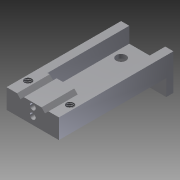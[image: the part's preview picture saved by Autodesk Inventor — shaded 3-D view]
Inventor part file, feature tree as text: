
AUTODESK INVENTOR PART (.ipt)
format: ipt  version: 2012 SP2 (Build 160219200, 219)  size: 177,152 bytes
history: native  units: in
note: dims shown in document units (in); Inventor stores cm internally (conversion verified against a paired STEP export)
features: extrude x8, sketch x8, thread x2
ambient origin geometry x8: Origin, YZ Plane, XZ Plane, XY Plane, X Axis, Y Axis, Z Axis, Center Point
bodies: Solid1 (feature_tree)
feature tree (18):
  extrude  "Extrusion1"  Depth=0.3in
  extrude  "Extrusion3"  Depth=0.4in
  sketch  "Sketch3"  dims[d4=0.5in d5=0.0in d6=0.09in]
  sketch  "Sketch4"  dims[d7=0.09in d8=0.06in]
  extrude  "Extrusion4"  Depth=0.09in
  extrude  "Extrusion5"  Depth=0.06in
  extrude  "Extrusion6"  Depth=0.075in
  thread  "Thread1"  [1 undecoded]
  thread  "Thread2"  [1 undecoded]
  extrude  "Extrusion9"  Depth=0.375in
  extrude  "Extrusion10"  TaperAngle=45.0deg  [1 undecoded]
  extrude  "Extrusion11"  TaperAngle=45.0deg  [1 undecoded]
  sketch  "Sketch1"  dims[d0=0.8in d1=0.3in]
  sketch  "Sketch2"  dims[d2=0.15in d3=0.4in]
  sketch  "Sketch5"  dims[d9=0.125in d10=0.075in d11=0.075in d12=0.0in]
  sketch  "Sketch8"  dims[d13=0.0in d14=0.375in]
  sketch  "Sketch9"  dims[d15=0.1875in d16=45.0deg]
  sketch  "Sketch10"  dims[d17=45.0deg d18=45.0deg d19=45.0deg d22=0.5in d23=0.0in d24=0.112in d25=0.25in d26=0.5in d27=0.112in d28=0.25in d29=0.1595in d30=0.0797in d31=0.1595in d32=0.0797in d33=0.5in d34=0.0in d35=0.5in d36=0.0in d37=0.125in d38=0.125in d39=0.0625in d40=1.25in d41=0.0in d42=1.0in d43=0.0in d44=1.0in d45=0.0in d58=0.11in d59=0.25in d60=0.0in d61=0.12in d62=0.8in d63=0.25in d64=0.125in d65=0.4in d66=0.3in d67=0.0in d68=0.15in d69=0.15in d70=0.125in d71=0.125in d72=1.0in d73=1.0in d74=0.3in d75=0.0in]
note: 4 required parameter values undecoded (feature->parameter linkage not recoverable at this tier; creation-order binding heuristic only, values carry confidence <= 0.55)
